# Revit family: DTI_A3-AC-Panel-B8-Carved-Frame-Fds6
name_source: partatom
category: Doors
revit_build: Autodesk Revit 2016 (Build: 20150220_1215(x64)
units: mm (PartAtom-declared; Revit-internal decimal feet)

## family parameters
Always vertical = Yes
Cut with Voids When Loaded = No
Host = Wall
Room Calculation Point = No
Shared = No

## types (1)
- Panel B8 Carved - Frame FDS6
    Assembly Code = B2030230
    Frame Depth = 47 mm  [stored 0.154199 ft]
    Frame Material = Meranti Wood
    Frame Thickness = 102 mm
    Frame Type = Frame FDS6
    Function = Interior
    Height = 2080 mm  [stored 6.82415 ft]
    Manufacturer = AC Doors
    Manufacturer Code = B8 Carved - FDS6
    Model = Double-sided Panel Door
    Panel Height = 2033 mm
    Panel Material = Meranti Wood
    Panel Thickness = 44 mm  [stored 0.144357 ft]
    Panel Type = B8 Carved
    Panel Width = 894 mm
    Sidelight Glass = Glass
    Sidelight w = 371 mm  [stored 1.21719 ft]
    URL = www.acdoors.co.za
    Wall Closure = By host
    Width = 1730 mm  [stored 5.67585 ft]

note: [stored X ft] marks values corroborated as IEEE doubles in the binary element streams (Revit-internal decimal feet)

## geometry (parser evidence)
native form markers: Sweep x7
no freeform markers — native parametric forms only
